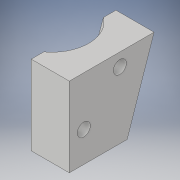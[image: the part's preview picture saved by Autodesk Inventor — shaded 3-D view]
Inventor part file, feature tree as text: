
AUTODESK INVENTOR PART (.ipt)
format: ipt  version: 2018 (Build 220112000, 112)  size: 182,272 bytes
history: native  units: in
note: dims shown in document units (in); Inventor stores cm internally (conversion verified against a paired STEP export)
features: sketch x8, extrude x4, loft x2, plane x1
ambient origin geometry x8: Origin, YZ Plane, XZ Plane, XY Plane, X Axis, Y Axis, Z Axis, Center Point
bodies: Solid1 (feature_tree)
feature tree (15):
  sketch  "Sketch1"  dims[d1=0.8in d2=1.2in]
  plane  "Work Plane1"
  loft  "Loft1"
  loft  "Loft2"
  extrude  "Extrusion1"  Depth=0.875in
  extrude  "Extrusion3"  TaperAngle=0.0deg  [1 undecoded]
  extrude  "Extrusion4"  Depth=1.6in
  extrude  "Extrusion5"  Depth=0.875in
  sketch  "Sketch3"  dims[d4=0.4in d5=2.8in]
  sketch  "Sketch4"  dims[d15=0.875in d17=0.875in]
  sketch  "Sketch5"  dims[d18=0.875in d19=0.0in d20=90.0deg]
  sketch  "Sketch6"  dims[d21=0.0in d22=90.0deg d23=1.6in]
  sketch  "Sketch8"  dims[d24=0.875in d26=0.875in]
  sketch  "Sketch9"  dims[d27=0.65in]
  sketch  "Sketch10"  dims[d28=0.0in d29=90.0deg d30=0.0in d31=90.0deg d32=0.4in d33=0.4in d34=0.4in d35=0.2in d36=0.0in d38=3.0in d39=0.0in d42=0.0in d43=0.25in d44=0.32in d46=0.18in d47=0.2in d48=0.18in d49=0.5in d50=0.5in d51=1.0in d52=0.0in d53=1.7in d54=0.0in d55=1.5in d56=0.0in d57=0.15in]
note: 1 required parameter value undecoded (feature->parameter linkage not recoverable at this tier; creation-order binding heuristic only, values carry confidence <= 0.55)
